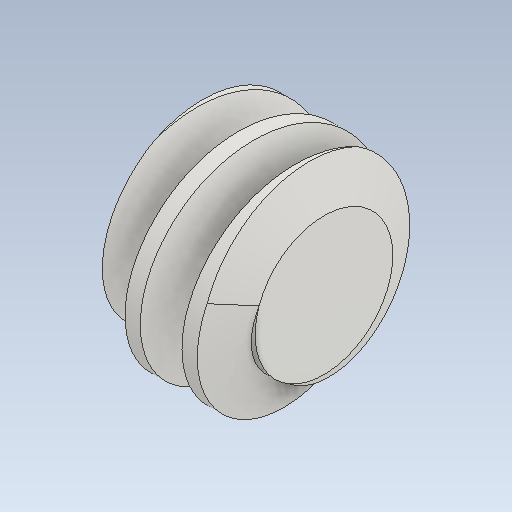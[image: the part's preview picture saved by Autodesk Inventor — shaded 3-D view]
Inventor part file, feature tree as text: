
AUTODESK INVENTOR PART (.ipt)
format: ipt  version: 2021 (Build 250183000, 183)  size: 228,864 bytes
history: native  units: mm (DEFAULTED — no unit token found)
features: other x6, chamfer x2, pattern_circular x2, extrude x1, sketch x1
ambient origin geometry x6: Origin, XZ Plane, X Axis, Y Axis, Z Axis, Center Point
bodies: Solid1 (feature_tree)
feature tree (12):
  extrude  "Base Body"  Depth=10.0mm
  chamfer  "Chamfer1"  Distance=30.0mm
  chamfer  "Chamfer2"  [1 undecoded]
  other  "Tooth Sketch"
  other  "Tooth"
  pattern_circular  "Tooth Pattern"  [2 undecoded]
  other  "Left Tooth"
  pattern_circular  "Left Tooth Pattern"  [2 undecoded]
  other  "Base Body Sketch"
  sketch  "Sketch5"  dims[d4=40.0mm d5=48.0mm d6=30.0mm d7=0.0mm d8=3.202938mm d9=8.8mm d10=3.202938mm d11=8.8mm d12=19.198622mm d14=3.1425mm d24=19.198622mm d25=31.415927mm d26=3.141593mm d27=15.2mm d28=20.0mm d29=24.24mm d30=12.566371mm d31=10.0mm d32=50.0mm d33=0.0mm d34=90.0deg d35=90.0deg d36=0.0mm d37=0.0mm d44=10.0mm d46=360.0deg d47=45.0deg d48=45.0deg d49=44.0mm d50=0.0mm d54=0.0mm d56=0.0mm d59=40.0mm d60=10.0mm d61=0.0mm d62=12.566371mm d63=10.0mm d64=50.0mm d65=0.0mm d66=90.0deg d67=90.0deg d68=0.0mm d69=0.0mm d70=10.0mm d71=10.0mm d72=10.0mm d73=360.0deg d75=10.0mm d76=10.0mm d77=0.0mm d79=44.0mm d80=0.0mm]
  other  "Srf1"
  other  "Pitch Diameter"
note: 5 required parameter values undecoded (feature->parameter linkage not recoverable at this tier; creation-order binding heuristic only, values carry confidence <= 0.55)
